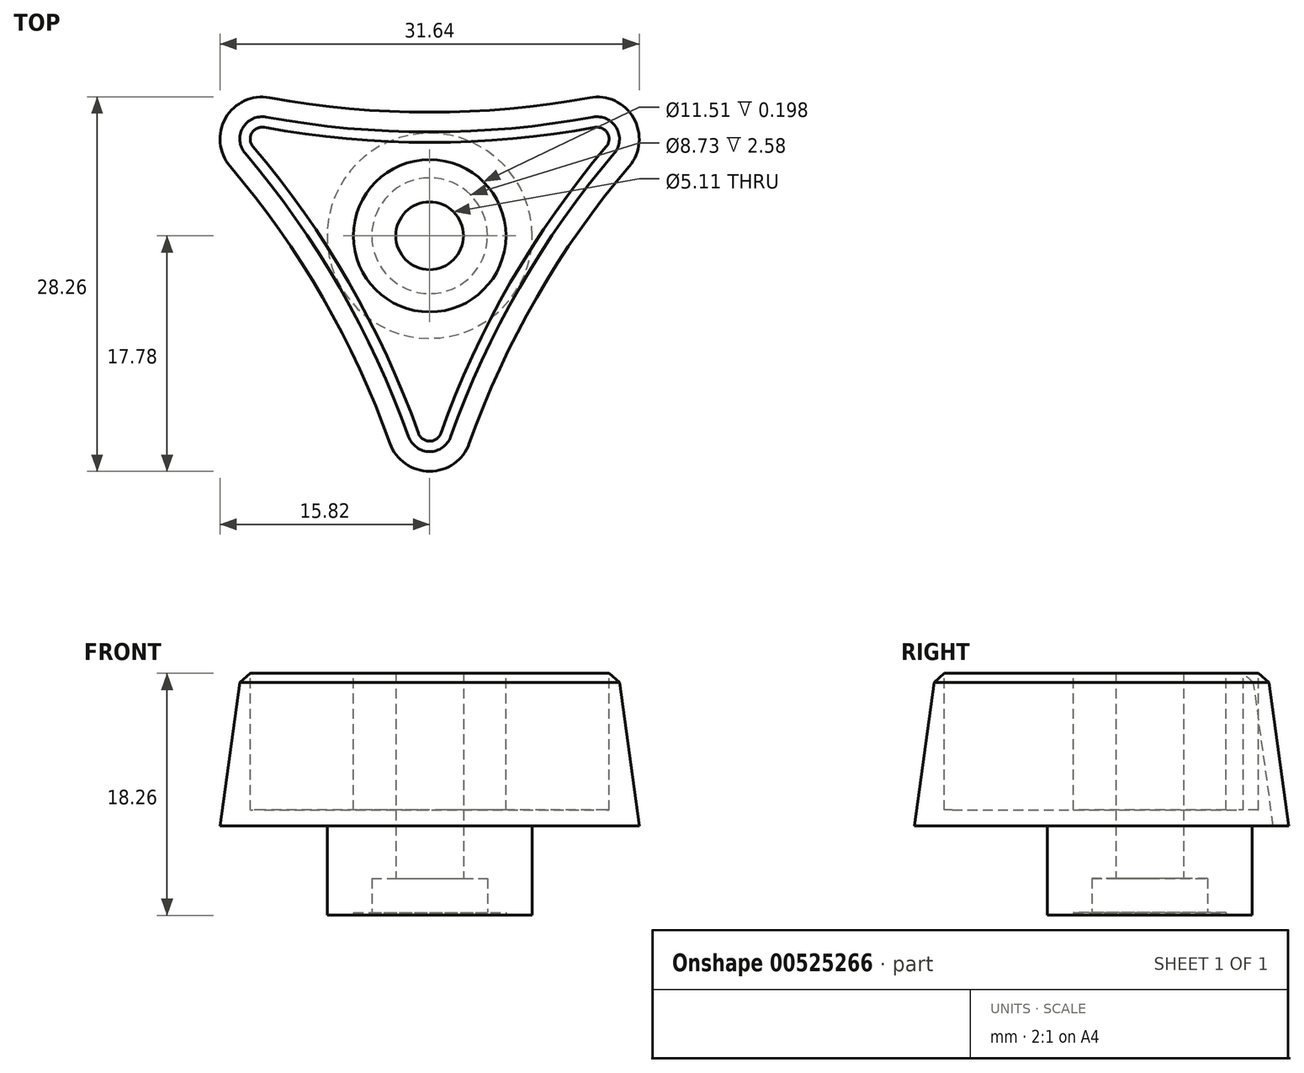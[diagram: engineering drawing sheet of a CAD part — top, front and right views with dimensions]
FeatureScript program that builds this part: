
annotation { "Feature Type Name" : "Feature", "Feature Type Description" : "" }
export const myFeature = defineFeature(function(context is Context, id is Id, definition is map)
    precondition{}
    {
        {
            var Q0;
            Q0=qCreatedBy(makeId("Top.planeOp"),FACE);
            var sketch = newSketch(context, id + "F0", { "sketchPlane" : qUnion([Q0])});
            skCircle(sketch, "E0", {"center": v(0, 0) * mm, "radius": 7.74 * mm, "construction": true});
            skLineSegment(sketch, "E1", {"start": v(0, 0) * mm, "end": v(0, 76.2) * mm, "construction": true});
            skLineSegment(sketch, "E2", {"start": v(0, 0) * mm, "end": v(66, -38.1) * mm, "construction": true});
            skLineSegment(sketch, "E3", {"start": v(0, 0) * mm, "end": v(-66, -38.1) * mm, "construction": true});
            skArc(sketch, "E4", {"start": v(13.86, 6.27) * mm, "mid": v(6.7, -3.87) * mm, "end": v(1.5, -15.14) * mm});
            skArc(sketch, "E5", {"start": v(-12.36, 8.86) * mm, "mid": v(0, 7.74) * mm, "end": v(12.36, 8.86) * mm});
            skArc(sketch, "E6.trimOffspring", {"start": v(-1.5, -15.14) * mm, "mid": v(-6.7, -3.87) * mm, "end": v(-13.86, 6.27) * mm});
            skPoint(sketch, "E7.visualSharp", {"position": v(-17.21, 9.94) * mm});
            skArc(sketch, "E7.filletArc", {"start": v(-12.36, 8.86) * mm, "mid": v(-14.02, 8.1) * mm, "end": v(-13.86, 6.27) * mm});
            skPoint(sketch, "E8.visualSharp", {"position": v(17.21, 9.94) * mm});
            skArc(sketch, "E8.filletArc", {"start": v(13.86, 6.27) * mm, "mid": v(14.02, 8.1) * mm, "end": v(12.36, 8.86) * mm});
            skPoint(sketch, "E9.visualSharp", {"position": v(0, -19.88) * mm});
            skArc(sketch, "E9.filletArc", {"start": v(-1.5, -15.14) * mm, "mid": v(0, -16.2) * mm, "end": v(1.5, -15.14) * mm});
            skSolve(sketch);
        }
        {
            var Q0;
            Q0=qCreatedBy(makeId("Top.planeOp"),FACE);
            cPlane(context, id + "F1", {"entities" : qUnion([Q0]), "cplaneType" : CPlaneType.OFFSET, "offset" : 11.5 * mm, "oppositeDirection" : true, "width" : 152.4 * mm, "height" : 152.4 * mm});
        }
        {
            var Q0;
            Q0=qCreatedBy(id+"F1.planeOp",FACE);
            var sketch = newSketch(context, id + "F2", { "sketchPlane" : qUnion([Q0])});
            skArc(sketch, "E10.0", {"start": v(-3, -15.67) * mm, "mid": v(0, -17.78) * mm, "end": v(3, -15.67) * mm});
            skArc(sketch, "E10.1", {"start": v(-12.08, 10.43) * mm, "mid": v(-15.4, 8.9) * mm, "end": v(-15.07, 5.25) * mm});
            skArc(sketch, "E10.2", {"start": v(-12.08, 10.43) * mm, "mid": v(0, 9.33) * mm, "end": v(12.08, 10.43) * mm});
            skArc(sketch, "E10.3", {"start": v(-3, -15.67) * mm, "mid": v(-8.08, -4.66) * mm, "end": v(-15.07, 5.25) * mm});
            skArc(sketch, "E10.4", {"start": v(15.07, 5.25) * mm, "mid": v(15.4, 8.9) * mm, "end": v(12.08, 10.43) * mm});
            skArc(sketch, "E10.5", {"start": v(15.07, 5.25) * mm, "mid": v(8.08, -4.66) * mm, "end": v(3, -15.67) * mm});
            skSolve(sketch);
        }
        {
            var Q0;
            Q0 = qSketchRegion(id + "F2", true);
            var Q1;
            Q1 = qSketchRegion(id + "F0", true);
            loft(context, id + "F3", {"sheetProfilesArray" : [{ "sheetProfileEntities" : qUnion([Q0]) }, { "sheetProfileEntities" : qUnion([Q1]) }]});
        }
        {
            var Q0;
            Q0=qCreatedBy(id+"F1.planeOp",FACE);
            var sketch = newSketch(context, id + "F4", { "sketchPlane" : qUnion([Q0])});
            skCircle(sketch, "E11.0", {"center": v(0, 0) * mm, "radius": 7.74 * mm});
            skSolve(sketch);
        }
        {
            var Q0;
            Q0 = qSketchRegion(id + "F4", true);
            var Q1;
            Q1=sQuery(id+"F4.wireOp",EDGE,"E11.0");
            extrude(context, id + "F5", {"entities" : qUnion([Q0]), "operationType" : NewBodyOperationType.ADD, "surfaceEntities" : qUnion([Q1]), "oppositeDirection" : true, "depth" : 6.75 * mm, "offsetDistance" : 25.4 * mm});
        }
        {
            var Q0;
            Q0=makeQuery(id+"F3.opLoft","MID_CAP_EDGE",EDGE,{"disambiguationData":[OSD([sQuery(id+"F0.wireOp",EDGE,"E5"),sQuery(id+"F0.wireOp",EDGE,"E7.filletArc"),sQuery(id+"F0.wireOp",EDGE,"E8.filletArc")])],"capPos":1.0});
            chamfer(context, id + "F6", {"entities" : qUnion([Q0]), "width" : 0.8 * mm, "tangentPropagation" : true});
        }
        {
            var Q0;
            Q0=makeQuery(id+"F5.opExtrude","CAP_FACE",FACE,{"disambiguationData":[OSD([sQuery(id+"F4.wireOp",EDGE,"E11.0")])],"isStart":false});
            var sketch = newSketch(context, id + "F7", { "sketchPlane" : qUnion([Q0])});
            skPoint(sketch, "E12", {"position": v(0, 0) * mm});
            skCircle(sketch, "E13", {"center": v(0, 0) * mm, "radius": 4.37 * mm});
            skCircle(sketch, "E14", {"center": v(0, 0) * mm, "radius": 5.75 * mm});
            skSolve(sketch);
        }
        {
            var Q0;
            Q0=makeQuery(id+"F7.imprint","IMPRINT",FACE,{"disambiguationData":[TD([[makeQuery(id+"F7.imprint","IMPRINT",EDGE,{"derivedFrom":sQuery(id+"F7.wireOp",EDGE,"E13")}),-1.0]])]});
            extrude(context, id + "F8", {"entities" : qUnion([Q0]), "operationType" : NewBodyOperationType.REMOVE, "oppositeDirection" : true, "depth" : 0.2 * mm, "offsetDistance" : 25.4 * mm});
        }
        {
            var Q0;
            Q0=makeQuery(id+"F7.imprint","IMPRINT",FACE,{"disambiguationData":[TD([[makeQuery(id+"F7.imprint","IMPRINT",EDGE,{"derivedFrom":sQuery(id+"F7.wireOp",EDGE,"E13")}),1.0]])]});
            extrude(context, id + "F9", {"entities" : qUnion([Q0]), "operationType" : NewBodyOperationType.REMOVE, "oppositeDirection" : true, "depth" : 2.78 * mm, "offsetDistance" : 25.4 * mm});
        }
        {
            var Q0;
            Q0=sQuery(id+"F7.wireOp",VERTEX,"E12");
            var Q1;
            Q1=makeQuery(id+"F3.opLoft","SWEPT_BODY",BODY,{"disambiguationData":[OSD([makeQuery(id+"F0.imprint","IMPRINT",FACE,{"disambiguationData":[TD([[makeQuery(id+"F0.imprint","IMPRINT",EDGE,{"derivedFrom":sQuery(id+"F0.wireOp",EDGE,"E4")}),-1.0]])]}),makeQuery(id+"F2.imprint","IMPRINT",FACE,{"disambiguationData":[TD([[makeQuery(id+"F2.imprint","IMPRINT",EDGE,{"derivedFrom":sQuery(id+"F2.wireOp",EDGE,"E10.0")}),1.0]])]})])]});
            hole(context, id + "F10", {"style" : HoleStyle.SIMPLE, "endStyle" : HoleEndStyle.THROUGH, "standardTappedOrClearance" : lookupTablePath({ "standard" : "ANSI", "engagement" : "75%", "pitch" : "20 tpi", "size" : "1/4", "type" : "Tapped" }), "standardBlindInLast" : lookupTablePath({ "standard" : "ANSI", "engagement" : "75%", "pitch" : "20 tpi", "size" : "1/4", "type" : "Tapped" }), "holeDiameter" : 5.1 * mm, "majorDiameter" : 6.35 * mm, "showTappedDepth" : true, "isTappedThrough" : true, "tappedDepth" : 12.7 * mm, "tapClearance" : 3, "locations" : qUnion([Q0]), "scope" : qUnion([Q1])});
        }
        {
            var Q0;
            Q0=makeQuery(id+"F3.opLoft","CAP_FACE",FACE,{"disambiguationData":[OSD([makeQuery(id+"F0.imprint","IMPRINT",FACE,{"disambiguationData":[TD([[makeQuery(id+"F0.imprint","IMPRINT",EDGE,{"derivedFrom":sQuery(id+"F0.wireOp",EDGE,"E4")}),-1.0]])]})])],"isStart":true});
            var sketch = newSketch(context, id + "F11", { "sketchPlane" : qUnion([Q0])});
            skCircle(sketch, "E15.0", {"center": v(0, 0) * mm, "radius": 5.75 * mm});
            skSolve(sketch);
        }
        {
            var Q0;
            Q0=makeQuery(id+"F11.imprint","IMPRINT",FACE,{"disambiguationData":[TD([[makeQuery(id+"F11.imprint","IMPRINT",EDGE,{"derivedFrom":sQuery(id+"F11.wireOp",EDGE,"E15.0")}),-1.0]])]});
            extrude(context, id + "F12", {"entities" : qUnion([Q0]), "operationType" : NewBodyOperationType.REMOVE, "oppositeDirection" : true, "depth" : 10.32 * mm, "offsetDistance" : 25.4 * mm});
        }
    });
